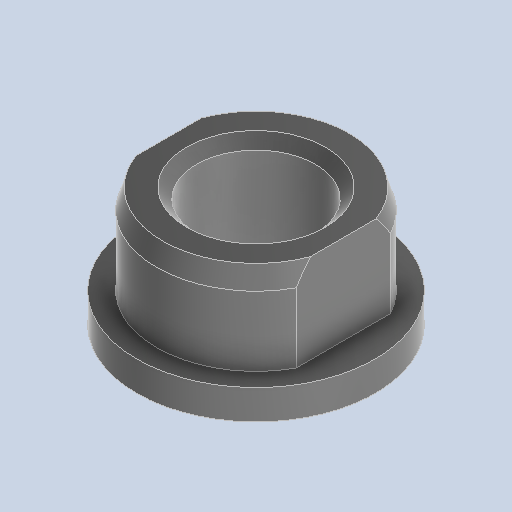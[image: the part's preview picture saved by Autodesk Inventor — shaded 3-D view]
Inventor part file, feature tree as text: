
AUTODESK INVENTOR PART (.ipt)
format: ipt  version: 2024.2 (Build 282272000, 272)  size: 158,208 bytes
history: native  units: mm
features: chamfer x3, sketch x2, revolve x1, extrude x1
ambient origin geometry x8: Origin, YZ Plane, XZ Plane, XY Plane, X Axis, Y Axis, Z Axis, Center Point
bodies: Solid1 (feature_tree)
feature tree (7):
  revolve  "Revolution1"  Angle=45.0deg
  chamfer  "Chamfer1"  Distance=1.0mm Angle=45.0deg
  chamfer  "Chamfer2"  Distance=10.0mm
  chamfer  "Chamfer3"  [1 undecoded]
  extrude  "Extrusion1"  [1 undecoded]
  sketch  "Sketch1"  dims[d5=90.0deg d7=2.0mm d8=45.0deg d16=1.0mm d11=45.0deg]
  sketch  "Sketch2"  dims[d14=45.0deg d18=10.0mm d0=0.0mm]
note: 2 required parameter values undecoded (feature->parameter linkage not recoverable at this tier; creation-order binding heuristic only, values carry confidence <= 0.55)
